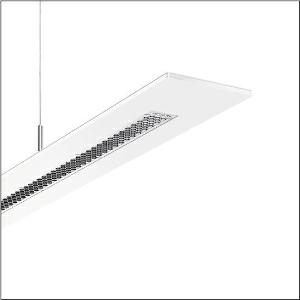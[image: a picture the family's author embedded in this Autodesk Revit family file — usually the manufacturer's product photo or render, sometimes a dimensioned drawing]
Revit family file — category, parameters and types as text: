
# Revit family: arktika_r__21_5mb251dl30840_e160
name_source: partatom
category: Lighting Fixtures
units: mm (PartAtom-declared; Revit-internal decimal feet)

## family parameters
Cut with Voids When Loaded = No
Host = Face
Light Source = No
Part Type = Normal
Room Calculation Point = No
Round Connector Dimension = Use Diameter
Shared = No

## types (1)
- --- (1 x LED 4000K / CRI = 80 (unbekannt), 4400 lm, 4000K)
    Apparent Load = 34 VA
    CIE Flux Codes = 81 100 100 79 100
    Color Rendering = 80
    Color Temperature = 4000K
    Default Elevation = 1800 mm
    Description = Arktika® 21, office luminaire, primary anti-glare with honeycomb louvre, of plastic, aluminium vaporised, highly specular, light emission: direct/indirect distribution, primary light characteristic: symmetric, installation type: suspended mounting, LED, rated luminous flux: 4.400lm, luminous efficacy: 131lm/W, light colour: 840, colour temperature: 4000K, control gear: ECG DALI, with terminal, 3+2-pole, max. 2.5mm², mains connection: 220..240V, AC, 50/60Hz, rated input power: 34W, housing, of aluminium, powder-coated, traffic white (RAL 9016), 1-length, length: 1.250mm, width: 120mm, height: 8mm, protection rating (complete): IP20, insulation class (complete): insulation class II (safety insulation), certification: CE, ENEC, VDE, packaging unit: 1 piece
    Height = 8 mm  [stored 0.0262467 ft]
    Lamp = 1 x LED 4000K / CRI >= 80 (unbekannt)
    Lamp Light Flux = 4400 lm
    Lamp count = 1
    Length = 1250 mm
    Luminous efficacy = 131 lm/W
    Manufacturer = Siteco
    ModVariant = No
    Model = 5MB251DL30840
    Mounting Place = Ceiling
    Mounting Type = Pendant
    Number of Poles = 1
    OnlyDefault = Yes
    Power Factor = 1
    Product Name = Arktika® 21
    Product group = office luminaire | ceiling pendant
    ProductGroupID = 902
    Protection Class = Protection class II
    Protection Degree = IP 20
    RLX_Detail_Level = 1
    RLX_Emergency_Light_Flux = 0 lm
    RLX_Emergency_Type = 0
    RLX_Emergency_Type_DB = No
    RlxData = <blob elided: 39329 chars, md5=bf8e9268>
    Socket = socket
    Standby Power = 0 W
    System Light Flux = 4400 lm
    System Power = 34 W
    Type Comments = factory setting: luminous flux: 100 % | dim-lin: 254 | 665 mA
    Type Image = l_1006128.jpg
    URL = http://relux.com
    VarID = @adj_148853
    Voltage = 0 V
    Weight = 0.00 kg
    Width = 120 mm

note: [stored X ft] marks values corroborated as IEEE doubles in the binary element streams (Revit-internal decimal feet)

## geometry (parser evidence)
native form markers: Blend x4, Sweep x10
no freeform markers — native parametric forms only
